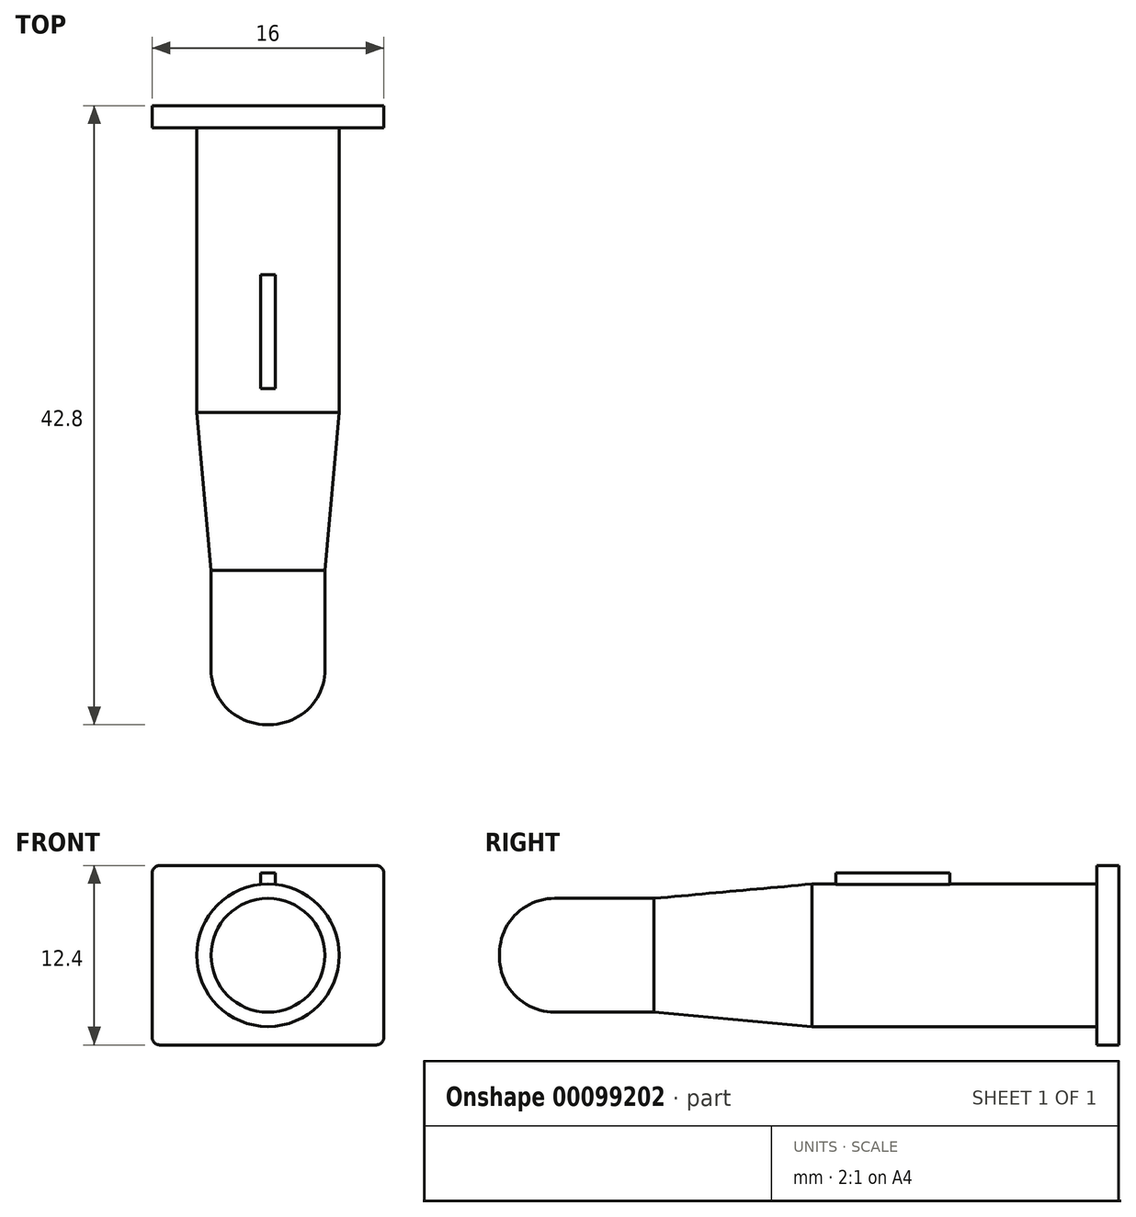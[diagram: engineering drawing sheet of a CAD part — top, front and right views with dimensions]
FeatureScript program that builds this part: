
annotation { "Feature Type Name" : "Feature", "Feature Type Description" : "" }
export const myFeature = defineFeature(function(context is Context, id is Id, definition is map)
    precondition{}
    {
        {
            var Q0;
            Q0=qCreatedBy(makeId("Front.planeOp"),FACE);
            var sketch = newSketch(context, id + "F3", { "sketchPlane" : qUnion([Q0])});
            skLineSegment(sketch, "E0.bottom", {"start": v(8, -6.2) * mm, "end": v(-8, -6.2) * mm});
            skLineSegment(sketch, "E0.top", {"start": v(8, 6.2) * mm, "end": v(-8, 6.2) * mm});
            skLineSegment(sketch, "E0.left", {"start": v(8, -6.2) * mm, "end": v(8, 6.2) * mm});
            skLineSegment(sketch, "E0.right", {"start": v(-8, -6.2) * mm, "end": v(-8, 6.2) * mm});
            skPoint(sketch, "E0.middle", {"position": v(0, 0) * mm});
            skSolve(sketch);
        }
        {
            var Q0;
            Q0 = qSketchRegion(id + "F3", true);
            extrude(context, id + "F4", {"entities" : qUnion([Q0]), "depth" : 1.52 * mm});
        }
        {
            var Q0;
            Q0=qCreatedBy(makeId("Right.planeOp"),FACE);
            var sketch = newSketch(context, id + "F0", { "sketchPlane" : qUnion([Q0])});
            skLineSegment(sketch, "E1", {"start": v(0, 0) * mm, "end": v(-42.8, 0) * mm});
            skLineSegment(sketch, "E2", {"start": v(-1.52, 0) * mm, "end": v(-1.52, 4.93) * mm});
            skLineSegment(sketch, "E3", {"start": v(-1.52, 4.93) * mm, "end": v(-21.2, 4.93) * mm});
            skLineSegment(sketch, "E4", {"start": v(-21.2, 4.93) * mm, "end": v(-32.13, 3.94) * mm});
            skLineSegment(sketch, "E5", {"start": v(-32.13, 3.94) * mm, "end": v(-42.8, 3.94) * mm});
            skLineSegment(sketch, "E6", {"start": v(-42.8, 3.94) * mm, "end": v(-42.8, 0) * mm});
            skSolve(sketch);
        }
        {
            var Q0;
            Q0 = qSketchRegion(id + "F0", true);
            var Q1;
            Q1=sQuery(id+"F0.wireOp",EDGE,"E1");
            revolve(context, id + "F5", {"operationType" : NewBodyOperationType.ADD, "entities" : qUnion([Q0]), "axis" : qUnion([Q1]), "revolveType" : RevolveType.FULL});
        }
        {
            var Q0;
            Q0=makeQuery(id+"F5.opRevolve","SWEPT_EDGE",EDGE,{"disambiguationData":[OSD([sQuery(id+"F0.wireOp",EDGE,"E5"),sQuery(id+"F0.wireOp",EDGE,"E6")])]});
            fillet(context, id + "F1", {"entities" : qUnion([Q0]), "radius" : 3.8 * mm, "tangentPropagation" : true, "allowEdgeOverflow" : false});
        }
        {
            var Q0;
            Q0=makeQuery(id+"F4.opExtrude","SWEPT_EDGE",EDGE,{"disambiguationData":[OSD([sQuery(id+"F3.wireOp",EDGE,"E0.top"),sQuery(id+"F3.wireOp",EDGE,"E0.left")])]});
            var Q1;
            Q1=makeQuery(id+"F4.opExtrude","SWEPT_EDGE",EDGE,{"disambiguationData":[OSD([sQuery(id+"F3.wireOp",EDGE,"E0.top"),sQuery(id+"F3.wireOp",EDGE,"E0.right")])]});
            var Q2;
            Q2=makeQuery(id+"F4.opExtrude","SWEPT_EDGE",EDGE,{"disambiguationData":[OSD([sQuery(id+"F3.wireOp",EDGE,"E0.bottom"),sQuery(id+"F3.wireOp",EDGE,"E0.right")])]});
            var Q3;
            Q3=makeQuery(id+"F4.opExtrude","SWEPT_EDGE",EDGE,{"disambiguationData":[OSD([sQuery(id+"F3.wireOp",EDGE,"E0.bottom"),sQuery(id+"F3.wireOp",EDGE,"E0.left")])]});
            fillet(context, id + "F6", {"entities" : qUnion([Q0, Q1, Q2, Q3]), "radius" : 0.5 * mm, "tangentPropagation" : true, "allowEdgeOverflow" : false});
        }
        {
            var Q0;
            Q0=qCreatedBy(makeId("Top.planeOp"),FACE);
            var sketch = newSketch(context, id + "F7", { "sketchPlane" : qUnion([Q0])});
            skLineSegment(sketch, "E7.bottom", {"start": v(0.5, -19.56) * mm, "end": v(-0.5, -19.56) * mm});
            skLineSegment(sketch, "E7.top", {"start": v(0.5, -11.68) * mm, "end": v(-0.5, -11.68) * mm});
            skLineSegment(sketch, "E7.left", {"start": v(0.5, -19.56) * mm, "end": v(0.5, -11.68) * mm});
            skLineSegment(sketch, "E7.right", {"start": v(-0.5, -19.56) * mm, "end": v(-0.5, -11.68) * mm});
            skPoint(sketch, "E7.middle", {"position": v(0, -15.62) * mm});
            skSolve(sketch);
        }
        {
            var Q0;
            Q0 = qSketchRegion(id + "F7", true);
            extrude(context, id + "F2", {"entities" : qUnion([Q0]), "operationType" : NewBodyOperationType.ADD, "depth" : 5.7 * mm});
        }
    });
